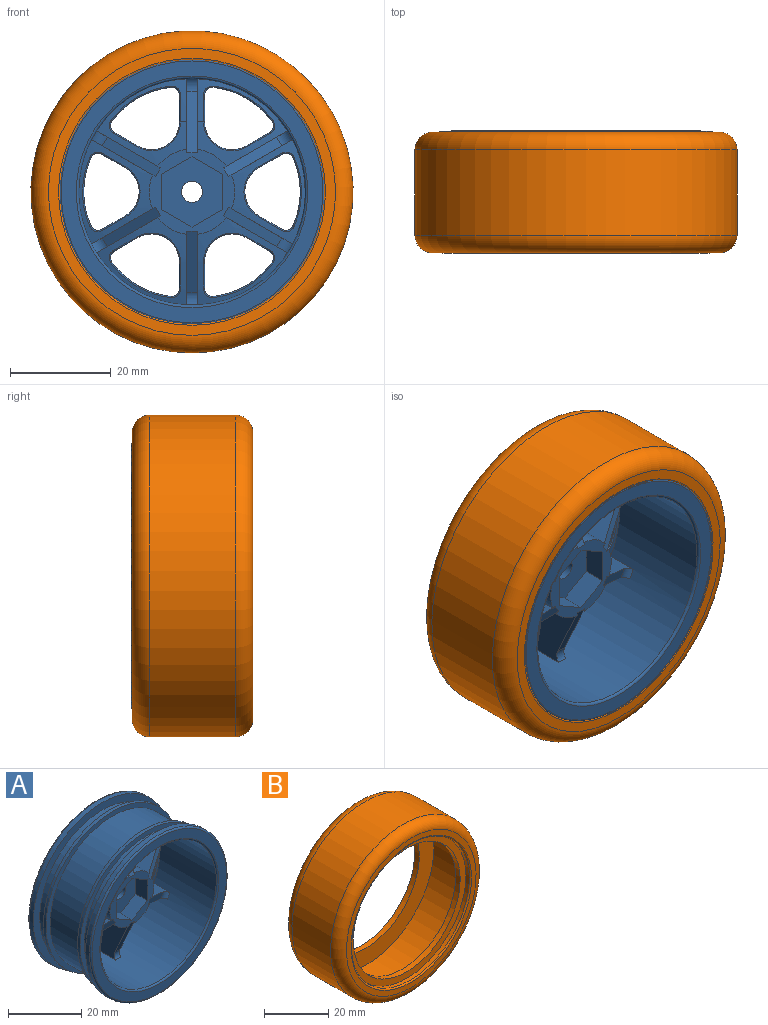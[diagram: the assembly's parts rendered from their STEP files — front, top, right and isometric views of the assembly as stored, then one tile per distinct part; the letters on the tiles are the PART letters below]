
ASSEMBLY  parts=2 mates=1
PART A: 203 faces, bbox 66.6x24.8x66.6 mm
  f0: plane 12.27x11.35mm, normal (-0.5,0,0.87), area 97.9mm2, adj f12,f32,f33,f58,f59,f60
  f1: plane 12.27x11.35mm, normal (-0.5,0,-0.87), area 97.9mm2, adj f12,f32,f33,f61,f62,f63
  f2: plane 14.15x11.35mm, normal (-1,0,0), area 97.9mm2, adj f32,f33,f34,f46,f47,f48
  f3: plane 12.27x11.35mm, normal (0.5,0,0.87), area 97.9mm2, adj f32,f33,f34,f61,f62,f63
  f4: plane 14.15x11.35mm, normal (-1,0,0), area 97.9mm2, adj f13,f32,f33,f55,f56,f57
  f5: plane 12.27x11.35mm, normal (0.5,0,-0.87), area 97.9mm2, adj f13,f32,f33,f58,f59,f60
  f6: plane 12.27x11.35mm, normal (-0.5,0,-0.87), area 97.9mm2, adj f14,f32,f33,f52,f53,f54
  f7: plane 14.15x11.35mm, normal (1,0,0), area 97.9mm2, adj f14,f32,f33,f55,f56,f57
  f8: plane 12.27x11.35mm, normal (0.5,0,-0.87), area 97.9mm2, adj f15,f32,f33,f49,f50,f51
  f9: plane 12.27x11.35mm, normal (0.5,0,0.87), area 97.9mm2, adj f15,f32,f33,f52,f53,f54
  f10: plane 14.15x11.35mm, normal (1,0,0), area 97.9mm2, adj f16,f32,f33,f46,f47,f48
  f11: plane 12.27x11.35mm, normal (-0.5,0,0.87), area 97.9mm2, adj f16,f32,f33,f49,f50,f51
  f12: cylinder r=8.5mm len=9.67mm, axis (0,1,0), area 66.7mm2, adj f0,f1,f33,f44,f201,f202
  f13: cylinder r=8.5mm len=9.67mm, axis (0,1,0), area 66.7mm2, adj f4,f5,f33,f44,f197,f198
  f14: cylinder r=8.5mm len=9.67mm, axis (0,1,0), area 66.7mm2, adj f6,f7,f33,f44,f195,f196
  f15: cylinder r=8.5mm len=9.67mm, axis (0,1,0), area 66.7mm2, adj f8,f9,f33,f44,f193,f194
  f16: cylinder r=8.5mm len=9.67mm, axis (0,1,0), area 66.7mm2, adj f10,f11,f33,f44,f191,f192
  f17: plane 52x52mm, normal (0,1,0), area 374.3mm2, adj f65,f68
  f18: cylinder r=26.5mm len=53mm, axis (0,1,0), area 249.8mm2, adj f19,f68
  f19: plane 53x53mm, normal (0,-1,0), area 396.6mm2, adj f18,f20
  f20: cylinder r=24mm len=48mm, axis (0,1,0), area 452.4mm2, adj f19,f21
  f21: plane 51.2x51.2mm, normal (0,1,0), area 249.3mm2, adj f20,f22
  f22: cylinder r=25.6mm len=51.2mm, axis (0,1,0), area 160.8mm2, adj f21,f23
  f23: plane 51.2x51.2mm, normal (0,-1,0), area 249.3mm2, adj f22,f24
  f24: cylinder r=24mm len=48mm, axis (0,1,0), area 1839.7mm2, adj f23,f25
  f25: plane 51.2x51.2mm, normal (0,1,0), area 249.3mm2, adj f24,f26
  f26: cylinder r=25.6mm len=51.2mm, axis (0,1,0), area 160.8mm2, adj f25,f27
  f27: plane 51.2x51.2mm, normal (0,-1,0), area 249.3mm2, adj f26,f28
  f28: cylinder r=24mm len=48mm, axis (0,1,0), area 452.4mm2, adj f27,f29
  f29: plane 53x53mm, normal (0,1,0), area 396.6mm2, adj f28,f30
  f30: cylinder r=26.5mm len=53mm, axis (0,1,0), area 249.8mm2, adj f29,f69
  f31: plane 52x52mm, normal (0,-1,0), area 461.8mm2, adj f69,f70
  f32: cylinder r=22.5mm len=45mm, axis (0,1,0), area 2992.3mm2, adj f0,f1,f2,f3,f4,f5,f6,f7
  f33: torus R=4.63mm, axis (0,1,0), area 527.7mm2, adj f0,f1,f2,f3,f4,f5,f6,f7
  f34: cylinder r=8.5mm len=9.67mm, axis (0,1,0), area 66.7mm2, adj f2,f3,f33,f44,f199,f200
  f35: plane 11x11mm, normal (0,1,0), area 81.2mm2, adj f64,f67
  f36: cylinder r=6.5mm len=13mm, axis (0,1,0), area 84.5mm2, adj f66,f67
  f37: torus R=4.63mm, axis (0,1,0), area 470.5mm2, adj f65,f66,f77,f78,f79,f80,f81,f82
  f38: plane 6.05x4.6mm, normal (0.5,0,0.87), area 32.1mm2, adj f39,f43,f44,f45
  f39: plane 6.99x4.6mm, normal (1,0,0), area 32.1mm2, adj f38,f40,f44,f45
  f40: plane 6.05x4.6mm, normal (0.5,0,-0.87), area 32.1mm2, adj f39,f41,f44,f45
  f41: plane 6.05x4.6mm, normal (-0.5,0,-0.87), area 32.1mm2, adj f40,f42,f44,f45
  f42: plane 6.99x4.6mm, normal (-1,0,0), area 32.1mm2, adj f41,f43,f44,f45
  f43: plane 6.05x4.6mm, normal (-0.5,0,0.87), area 32.1mm2, adj f38,f42,f44,f45
  f44: plane 17x16.88mm, normal (0,-1,0), area 92mm2, adj f12,f13,f14,f15,f16,f34,f38,f39
  f45: plane 13.97x12.1mm, normal (0,-1,0), area 112.9mm2, adj f38,f39,f40,f41,f42,f43,f64
  f46: cylinder r=2.31mm len=2.5mm, axis (-1,0,0), area 5.3mm2, adj f2,f10,f32,f48
  f47: cylinder r=79.95mm len=9.03mm, axis (-1,0,0), area 17.7mm2, adj f2,f10,f32,f33
  f48: plane 12.21x5.6mm, normal (0,-0.91,0.42), area 26.9mm2, adj f2,f10,f44,f46,f192,f200
  f49: cylinder r=2.31mm len=3.15mm, axis (-0.5,0,0.87), area 5.3mm2, adj f8,f11,f32,f51
  f50: cylinder r=79.95mm len=8.8mm, axis (-0.5,0,0.87), area 17.5mm2, adj f8,f11,f32,f33
  f51: plane 11.57x7.84mm, normal (0.36,-0.91,0.21), area 26.9mm2, adj f8,f11,f44,f49,f191,f194
  f52: cylinder r=2.31mm len=3.15mm, axis (0.5,0,0.87), area 5.3mm2, adj f6,f9,f32,f54
  f53: cylinder r=79.95mm len=8.8mm, axis (0.5,0,0.87), area 17.5mm2, adj f6,f9,f32,f33
  f54: plane 11.57x7.84mm, normal (0.36,-0.91,-0.21), area 26.9mm2, adj f6,f9,f44,f52,f193,f196
  f55: cylinder r=2.31mm len=2.48mm, axis (1,0,0), area 5.3mm2, adj f4,f7,f32,f57
  f56: cylinder r=79.95mm len=9.01mm, axis (1,0,0), area 17.5mm2, adj f4,f7,f32,f33
  f57: plane 12.21x5.6mm, normal (0,-0.91,-0.42), area 26.9mm2, adj f4,f7,f44,f55,f195,f198
  f58: cylinder r=2.31mm len=3.15mm, axis (0.5,0,-0.87), area 5.3mm2, adj f0,f5,f32,f60
  f59: cylinder r=79.95mm len=8.8mm, axis (0.5,0,-0.87), area 17.5mm2, adj f0,f5,f32,f33
  f60: plane 11.57x7.84mm, normal (-0.36,-0.91,-0.21), area 26.9mm2, adj f0,f5,f44,f58,f197,f202
  f61: cylinder r=2.31mm len=3.15mm, axis (-0.5,0,-0.87), area 5.3mm2, adj f1,f3,f32,f63
  f62: cylinder r=79.95mm len=8.8mm, axis (-0.5,0,-0.87), area 17.5mm2, adj f1,f3,f32,f33
  f63: plane 11.57x7.84mm, normal (-0.36,-0.91,0.21), area 26.9mm2, adj f1,f3,f44,f61,f199,f201
  f64: cylinder r=2.1mm len=4.2mm, axis (0,-1,0), area 26.4mm2, adj f35,f45
  f65: torus R=23.6mm, axis (0,-1,0), area 293.7mm2, adj f17,f37,f83,f103,f123,f143,f163,f183
  f66: torus R=8.5mm, axis (0,-1,0), area 137.6mm2, adj f36,f37
  f67: torus R=5.5mm, axis (0,-1,0), area 60.6mm2, adj f35,f36
  f68: torus R=26mm, axis (0,-1,0), area 129.9mm2, adj f17,f18
  f69: torus R=26mm, axis (0,1,0), area 129.9mm2, adj f30,f31
  f70: torus R=23mm, axis (0,1,0), area 111.9mm2, adj f31,f32
  f71: cylinder r=1.5mm len=2.18mm, axis (0,-1,0), area 4mm2, adj f75,f76,f82,f88
  f72: cylinder r=1.5mm len=1.99mm, axis (0,-1,0), area 4mm2, adj f73,f76,f79,f89
  f73: plane 5.42x2.42mm, normal (1,0,0), area 8.6mm2, adj f72,f74,f77,f87
  f74: cylinder r=5.5mm len=8.25mm, axis (0,-1,0), area 18.4mm2, adj f73,f75,f78,f85
  f75: plane 4.69x2.71mm, normal (-0.5,0,0.87), area 8.6mm2, adj f71,f74,f80,f86
  f76: cylinder r=16.65mm len=11.75mm, axis (0,-1,0), area 22.6mm2, adj f71,f72,f81,f83,f84,f90
  f77: bspline ~15.42x2.61mm, area 1.7mm2, adj f37,f73,f78,f79
  f78: bspline ~9.58x6.98mm, area 3.8mm2, adj f37,f74,f77,f80
  f79: bspline ~2.24x2.08mm, area 0.8mm2, adj f37,f72,f77,f81
  f80: bspline ~10.78x6.37mm, area 1.7mm2, adj f37,f75,f78,f82
  f81: bspline ~4.27x0.68mm, area 0.5mm2, adj f37,f76,f79,f83
  f82: bspline ~2.9x1.26mm, area 0.8mm2, adj f37,f71,f80,f84
  f83: bspline ~11.31x6.61mm, area 2.7mm2, adj f65,f76,f81,f84
  f84: bspline ~3.51x2.71mm, area 0.5mm2, adj f37,f76,f82,f83
  f85: bspline ~9.61x7mm, area 3.6mm2, adj f33,f74,f86,f87
  f86: bspline ~13.48x7.89mm, area 1.7mm2, adj f33,f75,f85,f88
  f87: bspline ~8.37x1.44mm, area 1.7mm2, adj f33,f73,f85,f89
  f88: bspline ~2.91x1.29mm, area 0.9mm2, adj f33,f71,f86,f90
  f89: bspline ~2.25x2.09mm, area 0.9mm2, adj f33,f72,f87,f90
  f90: bspline ~14.75x8.64mm, area 5mm2, adj f33,f76,f88,f89
  f91: cylinder r=1.5mm len=2.12mm, axis (0,-1,0), area 4mm2, adj f95,f96,f102,f108
  f92: cylinder r=1.5mm len=2.12mm, axis (0,-1,0), area 4mm2, adj f93,f96,f99,f109
  f93: plane 4.69x2.71mm, normal (0.5,0,-0.87), area 8.6mm2, adj f92,f94,f97,f107
  f94: cylinder r=5.5mm len=9.53mm, axis (0,-1,0), area 18.4mm2, adj f93,f95,f98,f105
  f95: plane 4.69x2.71mm, normal (0.5,0,0.87), area 8.6mm2, adj f91,f94,f100,f106
  f96: cylinder r=16.65mm len=13.56mm, axis (0,-1,0), area 22.6mm2, adj f91,f92,f101,f103,f104,f110
  f97: bspline ~13.45x7.86mm, area 1.7mm2, adj f37,f93,f98,f99
  f98: bspline ~10.9x4.11mm, area 3.8mm2, adj f37,f94,f97,f100
  f99: bspline ~2.82x1.39mm, area 0.8mm2, adj f37,f92,f97,f101
  f100: bspline ~10.82x6.34mm, area 1.7mm2, adj f37,f95,f98,f102
  f101: bspline ~4.01x1.81mm, area 0.5mm2, adj f37,f96,f99,f103
  f102: bspline ~2.82x1.39mm, area 0.8mm2, adj f37,f91,f100,f104
  f103: bspline ~13.04x1.46mm, area 2.7mm2, adj f65,f96,f101,f104
  f104: bspline ~4.01x1.81mm, area 0.5mm2, adj f37,f96,f102,f103
  f105: bspline ~10.94x4.11mm, area 3.6mm2, adj f33,f94,f106,f107
  f106: bspline ~13.47x7.9mm, area 1.7mm2, adj f33,f95,f105,f108
  f107: bspline ~10.83x6.37mm, area 1.7mm2, adj f33,f93,f105,f109
  f108: bspline ~2.61x1.42mm, area 0.9mm2, adj f33,f91,f106,f110
  f109: bspline ~2.84x1.42mm, area 0.9mm2, adj f33,f92,f107,f110
  f110: bspline ~15.81x2.51mm, area 5mm2, adj f33,f96,f108,f109
  f111: cylinder r=1.5mm len=1.99mm, axis (0,-1,0), area 4mm2, adj f115,f116,f122,f128
  f112: cylinder r=1.5mm len=2.18mm, axis (0,-1,0), area 4mm2, adj f113,f116,f119,f129
  f113: plane 4.69x2.71mm, normal (-0.5,0,-0.87), area 8.6mm2, adj f112,f114,f117,f127
  f114: cylinder r=5.5mm len=8.25mm, axis (0,-1,0), area 18.4mm2, adj f113,f115,f118,f125
  f115: plane 5.42x2.42mm, normal (1,0,0), area 8.6mm2, adj f111,f114,f120,f126
  f116: cylinder r=16.65mm len=11.75mm, axis (0,-1,0), area 22.6mm2, adj f111,f112,f121,f123,f124,f130
  f117: bspline ~10.43x6.16mm, area 1.7mm2, adj f37,f113,f118,f119
  f118: bspline ~9.58x6.97mm, area 3.8mm2, adj f37,f114,f117,f120
  f119: bspline ~2.9x1.26mm, area 0.8mm2, adj f37,f112,f117,f121
  f120: bspline ~12.38x2.37mm, area 1.7mm2, adj f37,f115,f118,f122
  f121: bspline ~3.51x2.71mm, area 0.5mm2, adj f37,f116,f119,f123
  f122: bspline ~2.24x2.08mm, area 0.8mm2, adj f37,f111,f120,f124
  f123: bspline ~11.31x6.61mm, area 2.7mm2, adj f65,f116,f121,f124
  f124: bspline ~4.27x0.68mm, area 0.5mm2, adj f37,f116,f122,f123
  f125: bspline ~9.61x7.01mm, area 3.6mm2, adj f33,f114,f126,f127
  f126: bspline ~11.42x1.69mm, area 1.7mm2, adj f33,f115,f125,f128
  f127: bspline ~10.84x6.36mm, area 1.7mm2, adj f33,f113,f125,f129
  f128: bspline ~2.25x2.09mm, area 0.9mm2, adj f33,f111,f126,f130
  f129: bspline ~2.91x1.29mm, area 0.9mm2, adj f33,f112,f127,f130
  f130: bspline ~14.75x8.64mm, area 5mm2, adj f33,f116,f128,f129
  f131: cylinder r=1.5mm len=2.18mm, axis (0,-1,0), area 4mm2, adj f135,f136,f142,f148
  f132: cylinder r=1.5mm len=1.99mm, axis (0,-1,0), area 4mm2, adj f133,f136,f139,f149
  f133: plane 5.42x2.42mm, normal (-1,0,0), area 8.6mm2, adj f132,f134,f137,f147
  f134: cylinder r=5.5mm len=8.25mm, axis (0,-1,0), area 18.4mm2, adj f133,f135,f138,f145
  f135: plane 4.69x2.71mm, normal (0.5,0,-0.87), area 8.6mm2, adj f131,f134,f140,f146
  f136: cylinder r=16.65mm len=11.75mm, axis (0,-1,0), area 22.6mm2, adj f131,f132,f141,f143,f144,f150
  f137: bspline ~15.42x2.61mm, area 1.7mm2, adj f37,f133,f138,f139
  f138: bspline ~9.58x6.98mm, area 3.8mm2, adj f37,f134,f137,f140
  f139: bspline ~2.24x2.08mm, area 0.8mm2, adj f37,f132,f137,f141
  f140: bspline ~10.78x6.37mm, area 1.7mm2, adj f37,f135,f138,f142
  f141: bspline ~4.27x0.68mm, area 0.5mm2, adj f37,f136,f139,f143
  f142: bspline ~2.9x1.26mm, area 0.8mm2, adj f37,f131,f140,f144
  f143: bspline ~11.31x6.61mm, area 2.7mm2, adj f65,f136,f141,f144
  f144: bspline ~3.51x2.71mm, area 0.5mm2, adj f37,f136,f142,f143
  f145: bspline ~9.61x7mm, area 3.6mm2, adj f33,f134,f146,f147
  f146: bspline ~13.48x7.89mm, area 1.7mm2, adj f33,f135,f145,f148
  f147: bspline ~8.37x1.44mm, area 1.7mm2, adj f33,f133,f145,f149
  f148: bspline ~2.91x1.29mm, area 0.9mm2, adj f33,f131,f146,f150
  f149: bspline ~2.25x2.09mm, area 0.9mm2, adj f33,f132,f147,f150
  f150: bspline ~14.75x8.64mm, area 5mm2, adj f33,f136,f148,f149
  f151: cylinder r=1.5mm len=2.12mm, axis (0,-1,0), area 4mm2, adj f155,f156,f162,f168
  f152: cylinder r=1.5mm len=2.12mm, axis (0,-1,0), area 4mm2, adj f153,f156,f159,f169
  f153: plane 4.69x2.71mm, normal (-0.5,0,0.87), area 8.6mm2, adj f152,f154,f157,f167
  f154: cylinder r=5.5mm len=9.53mm, axis (0,-1,0), area 18.4mm2, adj f153,f155,f158,f165
  f155: plane 4.69x2.71mm, normal (-0.5,0,-0.87), area 8.6mm2, adj f151,f154,f160,f166
  f156: cylinder r=16.65mm len=13.56mm, axis (0,-1,0), area 22.6mm2, adj f151,f152,f161,f163,f164,f170
  f157: bspline ~13.45x7.86mm, area 1.7mm2, adj f37,f153,f158,f159
  f158: bspline ~10.9x4.11mm, area 3.8mm2, adj f37,f154,f157,f160
  f159: bspline ~2.82x1.39mm, area 0.8mm2, adj f37,f152,f157,f161
  f160: bspline ~9.81x5.76mm, area 1.7mm2, adj f37,f155,f158,f162
  f161: bspline ~4.01x1.81mm, area 0.5mm2, adj f37,f156,f159,f163
  f162: bspline ~2.82x1.39mm, area 0.8mm2, adj f37,f151,f160,f164
  f163: bspline ~13.04x1.46mm, area 2.7mm2, adj f65,f156,f161,f164
  f164: bspline ~4.01x1.81mm, area 0.5mm2, adj f37,f156,f162,f163
  f165: bspline ~10.94x4.11mm, area 3.6mm2, adj f33,f154,f166,f167
  f166: bspline ~13.47x7.9mm, area 1.7mm2, adj f33,f155,f165,f168
  f167: bspline ~10.83x6.37mm, area 1.7mm2, adj f33,f153,f165,f169
  f168: bspline ~2.61x1.42mm, area 0.9mm2, adj f33,f151,f166,f170
  f169: bspline ~2.84x1.42mm, area 0.9mm2, adj f33,f152,f167,f170
  f170: bspline ~15.81x2.51mm, area 5mm2, adj f33,f156,f168,f169
  f171: cylinder r=1.5mm len=1.99mm, axis (0,-1,0), area 4mm2, adj f175,f176,f182,f188
  f172: cylinder r=1.5mm len=2.18mm, axis (0,-1,0), area 4mm2, adj f173,f176,f179,f189
  f173: plane 4.69x2.71mm, normal (0.5,0,0.87), area 8.6mm2, adj f172,f174,f177,f187
  f174: cylinder r=5.5mm len=8.25mm, axis (0,-1,0), area 18.4mm2, adj f173,f175,f178,f185
  f175: plane 5.42x2.42mm, normal (-1,0,0), area 8.6mm2, adj f171,f174,f180,f186
  f176: cylinder r=16.65mm len=11.75mm, axis (0,-1,0), area 22.6mm2, adj f171,f172,f181,f183,f184,f190
  f177: bspline ~13.41x7.88mm, area 1.7mm2, adj f37,f173,f178,f179
  f178: bspline ~9.58x6.97mm, area 3.8mm2, adj f37,f174,f177,f180
  f179: bspline ~2.9x1.26mm, area 0.8mm2, adj f37,f172,f177,f181
  f180: bspline ~12.38x2.37mm, area 1.7mm2, adj f37,f175,f178,f182
  f181: bspline ~3.51x2.71mm, area 0.5mm2, adj f37,f176,f179,f183
  f182: bspline ~2.24x2.08mm, area 0.8mm2, adj f37,f171,f180,f184
  f183: bspline ~11.31x6.61mm, area 2.7mm2, adj f65,f176,f181,f184
  f184: bspline ~5.6x1.08mm, area 0.5mm2, adj f37,f176,f182,f183
  f185: bspline ~9.61x7.01mm, area 3.6mm2, adj f33,f174,f186,f187
  f186: bspline ~11.42x1.69mm, area 1.7mm2, adj f33,f175,f185,f188
  f187: bspline ~10.84x6.36mm, area 1.7mm2, adj f33,f173,f185,f189
  f188: bspline ~2.25x2.09mm, area 0.9mm2, adj f33,f171,f186,f190
  f189: bspline ~2.8x1.06mm, area 0.9mm2, adj f33,f172,f187,f190
  f190: bspline ~14.75x8.64mm, area 5mm2, adj f33,f176,f188,f189
  f191: plane 0.56x0.32mm, normal (0.5,0,-0.87), area 0.1mm2, adj f16,f44,f51
  f192: plane 0.65x0.3mm, normal (-1,0,0), area 0.1mm2, adj f16,f44,f48
  f193: plane 0.56x0.32mm, normal (-0.5,0,-0.87), area 0.1mm2, adj f15,f44,f54
  f194: plane 0.56x0.32mm, normal (-0.5,0,0.87), area 0.1mm2, adj f15,f44,f51
  f195: plane 0.65x0.3mm, normal (-1,0,0), area 0.1mm2, adj f14,f44,f57
  f196: plane 0.56x0.32mm, normal (0.5,0,0.87), area 0.1mm2, adj f14,f44,f54
  f197: plane 0.56x0.32mm, normal (-0.5,0,0.87), area 0.1mm2, adj f13,f44,f60
  f198: plane 0.65x0.3mm, normal (1,0,0), area 0.1mm2, adj f13,f44,f57
  f199: plane 0.56x0.32mm, normal (-0.5,0,-0.87), area 0.1mm2, adj f34,f44,f63
  f200: plane 0.65x0.3mm, normal (1,0,0), area 0.1mm2, adj f34,f44,f48
  f201: plane 0.56x0.32mm, normal (0.5,0,0.87), area 0.1mm2, adj f12,f44,f63
  f202: plane 0.56x0.32mm, normal (0.5,0,-0.87), area 0.1mm2, adj f12,f44,f60
PART B: 16 faces, bbox 69.3x24x69.3 mm
  f0: torus R=28.5mm, axis (0,-1,0), area 1061.5mm2, adj f1,f15
  f1: cylinder r=32mm len=64mm, axis (0,-1,0), area 3418.1mm2, adj f0,f2
  f2: torus R=28.5mm, axis (0,-1,0), area 1061.5mm2, adj f1,f3
  f3: plane 57x57mm, normal (0,-1,0), area 345.6mm2, adj f2,f4
  f4: torus R=26.5mm, axis (0,-1,0), area 129.2mm2, adj f3,f5
  f5: cylinder r=26mm len=52mm, axis (0,-1,0), area 245mm2, adj f4,f6
  f6: plane 52x52mm, normal (0,-1,0), area 388.8mm2, adj f5,f7
  f7: cylinder r=23.5mm len=47mm, axis (0,-1,0), area 295.3mm2, adj f6,f8
  f8: plane 60x60mm, normal (0,1,0), area 1092.5mm2, adj f7,f9
  f9: cylinder r=30mm len=60mm, axis (0,-1,0), area 3015.9mm2, adj f8,f10
  f10: plane 60x60mm, normal (0,-1,0), area 1092.5mm2, adj f9,f11
  f11: cylinder r=23.5mm len=47mm, axis (0,-1,0), area 295.3mm2, adj f10,f12
  f12: plane 52x52mm, normal (0,1,0), area 388.8mm2, adj f11,f13
  f13: cylinder r=26mm len=52mm, axis (0,-1,0), area 245mm2, adj f12,f14
  f14: torus R=26.5mm, axis (0,-1,0), area 129.2mm2, adj f13,f15
  f15: plane 57x57mm, normal (0,1,0), area 345.6mm2, adj f0,f14
PLACE A at identity fixed
PLACE B t=(0,-0.1,0)mm
MATE fastened B.f0 <-> A.f12  axis (0,-1,0) through (0,-10.1,0)mm
